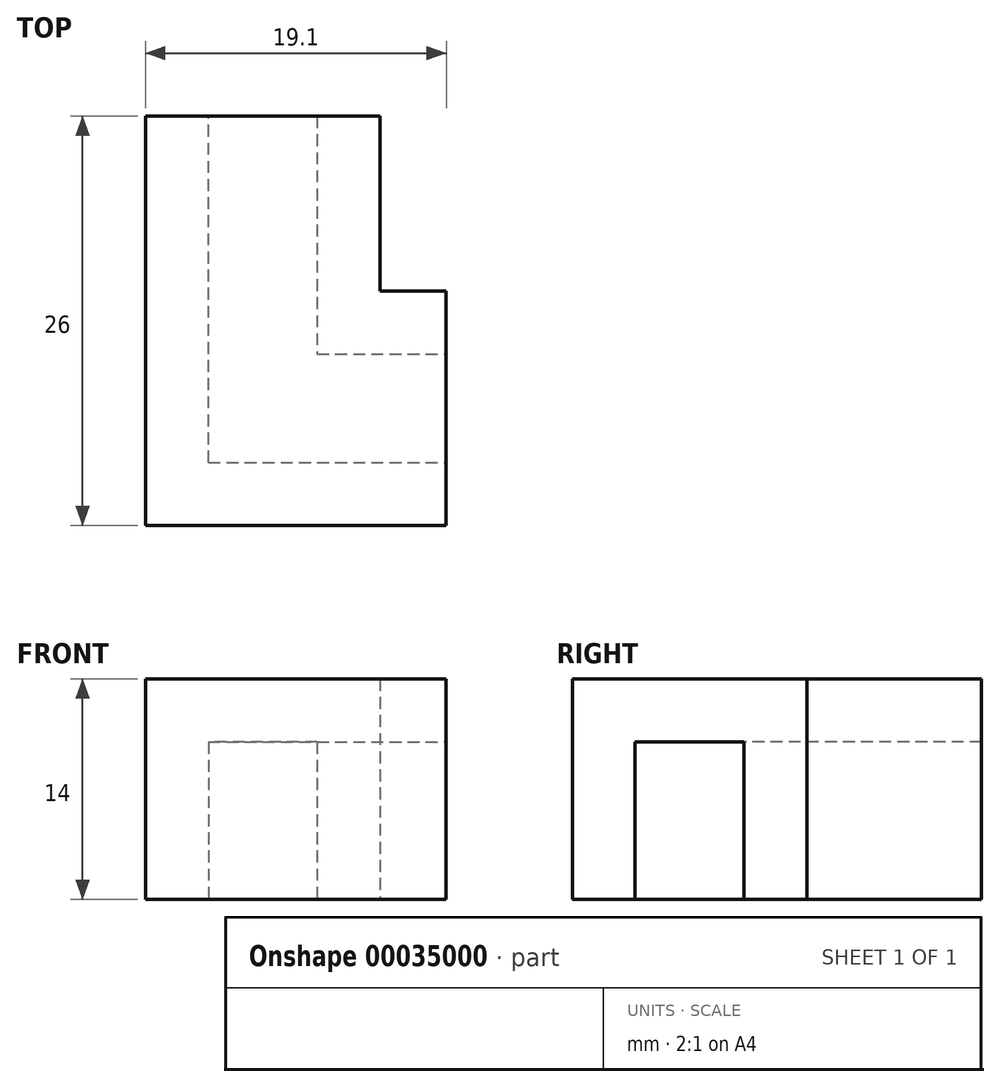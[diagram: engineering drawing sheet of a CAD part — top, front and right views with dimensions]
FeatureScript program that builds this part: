
annotation { "Feature Type Name" : "Feature", "Feature Type Description" : "" }
export const myFeature = defineFeature(function(context is Context, id is Id, definition is map)
    precondition{}
    {
        {
            var Q0;
            Q0=qCreatedBy(makeId("Top.planeOp"),FACE);
            var sketch = newSketch(context, id + "F0", { "sketchPlane" : qUnion([Q0])});
            skLineSegment(sketch, "E0.bottom", {"start": v(-48, 33.13) * mm, "end": v(-44, 33.13) * mm});
            skLineSegment(sketch, "E0.left", {"start": v(-48, 33.13) * mm, "end": v(-48, 18.03) * mm});
            skLineSegment(sketch, "E1.top", {"start": v(-48, 18.03) * mm, "end": v(-39.8, 18.03) * mm});
            skLineSegment(sketch, "E1.right", {"start": v(-39.8, 22.03) * mm, "end": v(-39.8, 18.03) * mm});
            skLineSegment(sketch, "E2.bottom", {"start": v(-54.9, 33.13) * mm, "end": v(-58.9, 33.13) * mm});
            skLineSegment(sketch, "E2.top", {"start": v(-39.8, 7.13) * mm, "end": v(-58.9, 7.13) * mm});
            skLineSegment(sketch, "E2.right", {"start": v(-58.9, 33.13) * mm, "end": v(-58.9, 7.13) * mm});
            skLineSegment(sketch, "E3.top", {"start": v(-54.9, 11.13) * mm, "end": v(-39.8, 11.13) * mm});
            skLineSegment(sketch, "E3.right", {"start": v(-39.8, 7.13) * mm, "end": v(-39.8, 11.13) * mm});
            skLineSegment(sketch, "E4", {"start": v(-54.9, 11.13) * mm, "end": v(-54.9, 11.13) * mm});
            skLineSegment(sketch, "E5", {"start": v(-44, 22.03) * mm, "end": v(-39.8, 22.03) * mm});
            skLineSegment(sketch, "E6", {"start": v(-44, 22.03) * mm, "end": v(-44, 33.13) * mm});
            skLineSegment(sketch, "E7", {"start": v(-54.9, 11.13) * mm, "end": v(-54.9, 33.13) * mm});
            skLineSegment(sketch, "E8", {"start": v(-39.8, 11.13) * mm, "end": v(-39.8, 18.03) * mm, "construction": true});
            skSolve(sketch);
        }
        {
            var Q0;
            Q0=makeQuery(id+"F0.imprint","IMPRINT",FACE,{"disambiguationData":[TD([[makeQuery(id+"F0.imprint","IMPRINT",EDGE,{"derivedFrom":sQuery(id+"F0.wireOp",EDGE,"E2.bottom")}),1.0]])]});
            var Q1;
            Q1=makeQuery(id+"F0.imprint","IMPRINT",FACE,{"disambiguationData":[TD([[makeQuery(id+"F0.imprint","IMPRINT",EDGE,{"derivedFrom":sQuery(id+"F0.wireOp",EDGE,"E0.bottom")}),-1.0]])]});
            extrude(context, id + "F1", {"entities" : qUnion([Q0, Q1]), "depth" : 10 * mm});
        }
        {
            var Q0;
            Q0=makeQuery(id+"F1.opExtrude","CAP_FACE",FACE,{"disambiguationData":[OSD([sQuery(id+"F0.wireOp",EDGE,"E2.bottom"),sQuery(id+"F0.wireOp",EDGE,"E2.top"),sQuery(id+"F0.wireOp",EDGE,"E2.left"),sQuery(id+"F0.wireOp",EDGE,"E2.right"),sQuery(id+"F0.wireOp",EDGE,"E3.top"),sQuery(id+"F0.wireOp",EDGE,"E3.right")])],"isStart":false});
            var sketch = newSketch(context, id + "F2", { "sketchPlane" : qUnion([Q0])});
            skLineSegment(sketch, "E9.0", {"start": v(-39.8, 7.13) * mm, "end": v(-58.9, 7.13) * mm});
            skLineSegment(sketch, "E10.0", {"start": v(-58.9, 33.13) * mm, "end": v(-58.9, 7.13) * mm});
            skLineSegment(sketch, "E11.0", {"start": v(-44, 22.03) * mm, "end": v(-44, 33.13) * mm});
            skPoint(sketch, "E12.0", {"position": v(-41.9, 22.03) * mm});
            skLineSegment(sketch, "E13", {"start": v(-39.8, 7.13) * mm, "end": v(-39.8, 22.03) * mm});
            skLineSegment(sketch, "E14", {"start": v(-58.9, 33.13) * mm, "end": v(-44, 33.13) * mm});
            skLineSegment(sketch, "E15", {"start": v(-44, 22.03) * mm, "end": v(-39.8, 22.03) * mm});
            skSolve(sketch);
        }
        {
            var Q0;
            Q0 = qSketchRegion(id + "F2", true);
            extrude(context, id + "F3", {"entities" : qUnion([Q0]), "operationType" : NewBodyOperationType.ADD, "depth" : 4 * mm});
        }
    });
